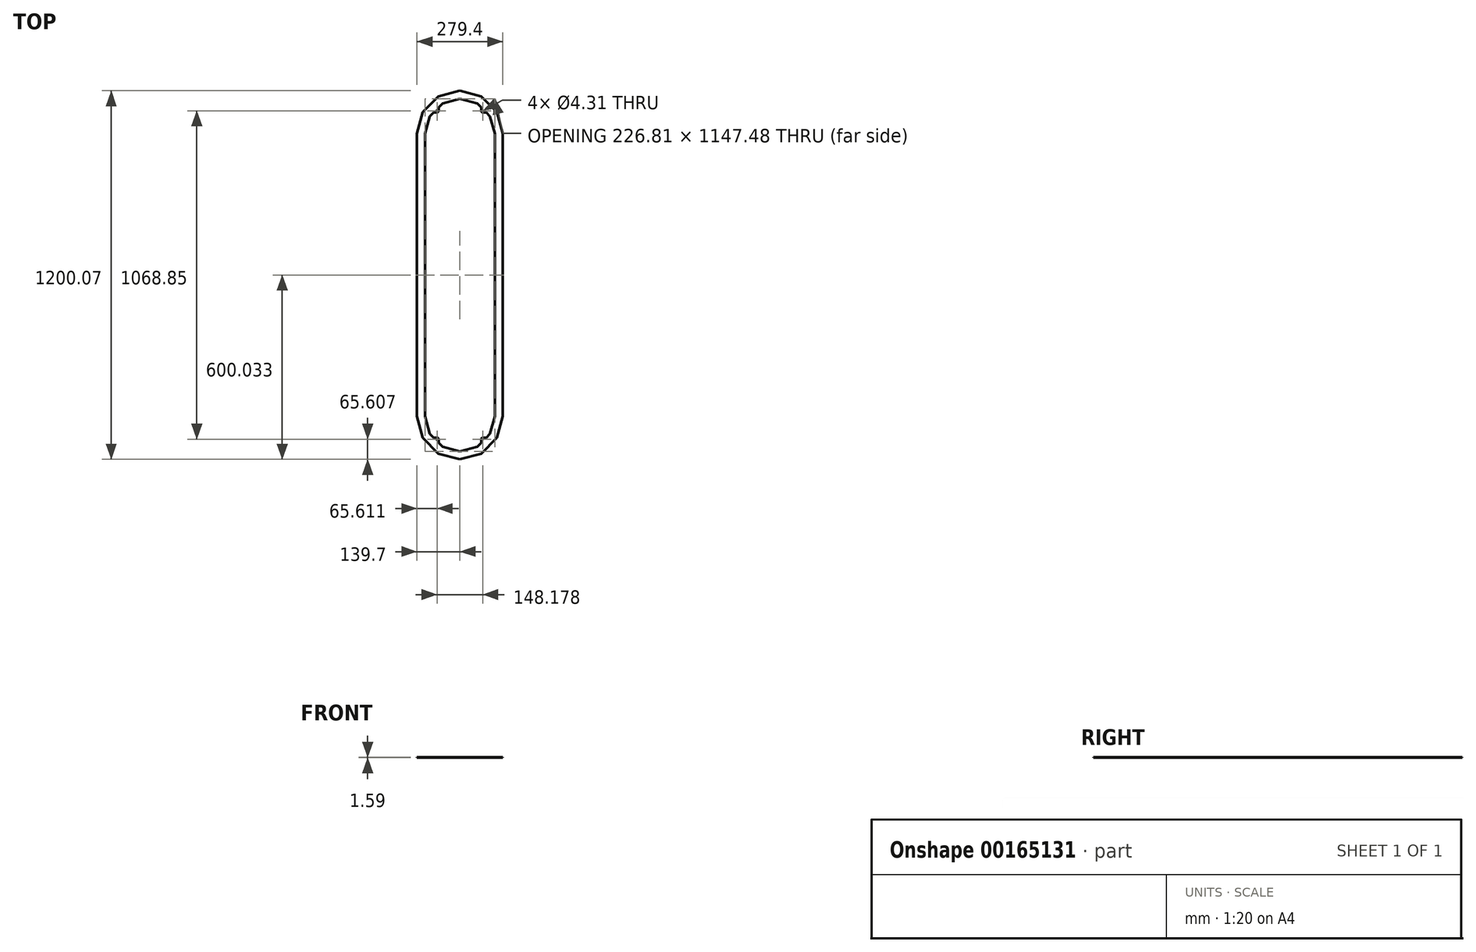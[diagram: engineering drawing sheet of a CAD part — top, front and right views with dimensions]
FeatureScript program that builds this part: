
annotation { "Feature Type Name" : "Feature", "Feature Type Description" : "" }
export const myFeature = defineFeature(function(context is Context, id is Id, definition is map)
    precondition{}
    {
        {
            var Q0;
            Q0=qCreatedBy(makeId("Top.planeOp"),FACE);
            var sketch = newSketch(context, id + "F0", { "sketchPlane" : qUnion([Q0])});
            skLineSegment(sketch, "E0", {"start": v(139.7, 0) * mm, "end": v(279.4, 0) * mm, "construction": true});
            skLineSegment(sketch, "E1", {"start": v(139.7, 0) * mm, "end": v(260.68, 69.85) * mm, "construction": true});
            skLineSegment(sketch, "E2", {"start": v(139.7, 0) * mm, "end": v(209.55, 120.98) * mm, "construction": true});
            skLineSegment(sketch, "E3", {"start": v(139.7, 0) * mm, "end": v(139.7, 139.7) * mm, "construction": true});
            skLineSegment(sketch, "E4", {"start": v(279.4, 0) * mm, "end": v(260.68, 69.85) * mm});
            skLineSegment(sketch, "E5", {"start": v(260.68, 69.85) * mm, "end": v(209.55, 120.98) * mm});
            skLineSegment(sketch, "E6", {"start": v(209.55, 120.98) * mm, "end": v(139.7, 139.7) * mm});
            skLineSegment(sketch, "E7", {"start": v(279.4, 0) * mm, "end": v(279.4, -920.67) * mm});
            skLineSegment(sketch, "E8", {"start": v(279.4, -920.67) * mm, "end": v(139.7, -920.67) * mm, "construction": true});
            skLineSegment(sketch, "E9", {"start": v(139.7, -920.67) * mm, "end": v(260.68, -990.52) * mm, "construction": true});
            skLineSegment(sketch, "E10", {"start": v(139.7, 0) * mm, "end": v(69.85, 120.98) * mm, "construction": true});
            skLineSegment(sketch, "E11", {"start": v(139.7, 0) * mm, "end": v(18.72, 69.85) * mm, "construction": true});
            skLineSegment(sketch, "E12", {"start": v(139.7, 0) * mm, "end": v(0, 0) * mm, "construction": true});
            skLineSegment(sketch, "E13", {"start": v(139.7, -920.67) * mm, "end": v(0, -920.67) * mm, "construction": true});
            skLineSegment(sketch, "E14", {"start": v(139.7, 139.7) * mm, "end": v(69.85, 120.98) * mm});
            skLineSegment(sketch, "E15", {"start": v(69.85, 120.98) * mm, "end": v(18.72, 69.85) * mm});
            skLineSegment(sketch, "E16", {"start": v(18.72, 69.85) * mm, "end": v(0, 0) * mm});
            skLineSegment(sketch, "E17", {"start": v(0, 0) * mm, "end": v(0, -920.67) * mm});
            skLineSegment(sketch, "E18", {"start": v(139.7, -920.67) * mm, "end": v(209.55, -1041.66) * mm, "construction": true});
            skLineSegment(sketch, "E19", {"start": v(139.7, -920.67) * mm, "end": v(139.7, -1060.37) * mm, "construction": true});
            skLineSegment(sketch, "E20", {"start": v(139.7, -920.67) * mm, "end": v(69.85, -1041.66) * mm, "construction": true});
            skLineSegment(sketch, "E21", {"start": v(139.7, -920.67) * mm, "end": v(18.72, -990.52) * mm, "construction": true});
            skLineSegment(sketch, "E22", {"start": v(0, -920.67) * mm, "end": v(18.72, -990.52) * mm});
            skLineSegment(sketch, "E23", {"start": v(18.72, -990.52) * mm, "end": v(69.85, -1041.66) * mm});
            skLineSegment(sketch, "E24", {"start": v(69.85, -1041.66) * mm, "end": v(139.7, -1060.37) * mm});
            skLineSegment(sketch, "E25", {"start": v(139.7, -1060.37) * mm, "end": v(209.55, -1041.66) * mm});
            skLineSegment(sketch, "E26", {"start": v(209.55, -1041.66) * mm, "end": v(260.68, -990.52) * mm});
            skLineSegment(sketch, "E27", {"start": v(260.68, -990.52) * mm, "end": v(279.4, -920.67) * mm});
            skLineSegment(sketch, "E28", {"start": v(139.7, 0) * mm, "end": v(139.7, -460.34) * mm, "construction": true});
            skLineSegment(sketch, "E29", {"start": v(139.7, -460.34) * mm, "end": v(139.7, -920.67) * mm, "construction": true});
            skSolve(sketch);
        }
        {
            var Q0;
            Q0=qSketchRegion(id+"F0",true);
            extrude(context, id + "F1", {"entities" : qUnion([Q0]), "depth" : 1.59 * mm});
        }
        {
            var Q0;
            Q0=makeQuery(id+"F1.opExtrude","CAP_FACE",FACE,{"disambiguationData":[OSD([sQuery(id+"F0.wireOp",EDGE,"E4"),sQuery(id+"F0.wireOp",EDGE,"E5"),sQuery(id+"F0.wireOp",EDGE,"E6"),sQuery(id+"F0.wireOp",EDGE,"E7"),sQuery(id+"F0.wireOp",EDGE,"E14"),sQuery(id+"F0.wireOp",EDGE,"E15"),sQuery(id+"F0.wireOp",EDGE,"E16"),sQuery(id+"F0.wireOp",EDGE,"E17"),sQuery(id+"F0.wireOp",EDGE,"E22"),sQuery(id+"F0.wireOp",EDGE,"E23"),sQuery(id+"F0.wireOp",EDGE,"E24"),sQuery(id+"F0.wireOp",EDGE,"E25"),sQuery(id+"F0.wireOp",EDGE,"E26"),sQuery(id+"F0.wireOp",EDGE,"E27")])],"isStart":false});
            var sketch = newSketch(context, id + "F2", { "sketchPlane" : qUnion([Q0])});
            skLineSegment(sketch, "E30", {"start": v(139.7, 0) * mm, "end": v(253.1, 0) * mm, "construction": true});
            skLineSegment(sketch, "E31", {"start": v(139.7, 0) * mm, "end": v(237.91, 56.7) * mm, "construction": true});
            skLineSegment(sketch, "E32", {"start": v(139.7, 0) * mm, "end": v(196.4, 98.21) * mm, "construction": true});
            skLineSegment(sketch, "E33", {"start": v(139.7, 0) * mm, "end": v(139.7, 113.4) * mm, "construction": true});
            skLineSegment(sketch, "E34", {"start": v(253.1, 0) * mm, "end": v(237.91, 56.7) * mm});
            skLineSegment(sketch, "E35", {"start": v(237.91, 56.7) * mm, "end": v(196.4, 98.21) * mm});
            skLineSegment(sketch, "E36", {"start": v(196.4, 98.21) * mm, "end": v(139.7, 113.4) * mm});
            skLineSegment(sketch, "E37", {"start": v(253.1, 0) * mm, "end": v(253.1, -920.67) * mm});
            skLineSegment(sketch, "E38", {"start": v(253.1, -920.67) * mm, "end": v(139.7, -920.67) * mm, "construction": true});
            skLineSegment(sketch, "E39", {"start": v(139.7, -920.67) * mm, "end": v(237.91, -977.38) * mm, "construction": true});
            skLineSegment(sketch, "E40", {"start": v(139.7, 0) * mm, "end": v(83, 98.21) * mm, "construction": true});
            skLineSegment(sketch, "E41", {"start": v(139.7, 0) * mm, "end": v(41.49, 56.7) * mm, "construction": true});
            skLineSegment(sketch, "E42", {"start": v(139.7, 0) * mm, "end": v(26.3, 0) * mm, "construction": true});
            skLineSegment(sketch, "E43", {"start": v(139.7, -920.67) * mm, "end": v(26.3, -920.67) * mm, "construction": true});
            skLineSegment(sketch, "E44", {"start": v(139.7, 113.4) * mm, "end": v(83, 98.21) * mm});
            skLineSegment(sketch, "E45", {"start": v(83, 98.21) * mm, "end": v(41.49, 56.7) * mm});
            skLineSegment(sketch, "E46", {"start": v(41.49, 56.7) * mm, "end": v(26.3, 0) * mm});
            skLineSegment(sketch, "E47", {"start": v(26.3, 0) * mm, "end": v(26.3, -920.67) * mm});
            skLineSegment(sketch, "E48", {"start": v(139.7, -920.67) * mm, "end": v(196.4, -1018.89) * mm, "construction": true});
            skLineSegment(sketch, "E49", {"start": v(139.7, -920.67) * mm, "end": v(139.7, -1034.08) * mm, "construction": true});
            skLineSegment(sketch, "E50", {"start": v(139.7, -920.67) * mm, "end": v(83, -1018.89) * mm, "construction": true});
            skLineSegment(sketch, "E51", {"start": v(139.7, -920.67) * mm, "end": v(41.49, -977.38) * mm, "construction": true});
            skLineSegment(sketch, "E52", {"start": v(26.3, -920.67) * mm, "end": v(41.49, -977.38) * mm});
            skLineSegment(sketch, "E53", {"start": v(41.49, -977.38) * mm, "end": v(83, -1018.89) * mm});
            skLineSegment(sketch, "E54", {"start": v(83, -1018.89) * mm, "end": v(139.7, -1034.08) * mm});
            skLineSegment(sketch, "E55", {"start": v(139.7, -1034.08) * mm, "end": v(196.4, -1018.89) * mm});
            skLineSegment(sketch, "E56", {"start": v(196.4, -1018.89) * mm, "end": v(237.91, -977.38) * mm});
            skLineSegment(sketch, "E57", {"start": v(237.91, -977.38) * mm, "end": v(253.1, -920.67) * mm});
            skLineSegment(sketch, "E58", {"start": v(139.7, 0) * mm, "end": v(139.7, -460.34) * mm, "construction": true});
            skLineSegment(sketch, "E59", {"start": v(139.7, -460.34) * mm, "end": v(139.7, -920.67) * mm, "construction": true});
            skLineSegment(sketch, "E60", {"start": v(33.9, 28.35) * mm, "end": v(9.36, 34.93) * mm, "construction": true});
            skLineSegment(sketch, "E61", {"start": v(245.5, 28.35) * mm, "end": v(270.04, 34.93) * mm, "construction": true});
            skLineSegment(sketch, "E62", {"start": v(33.9, -949.03) * mm, "end": v(9.36, -955.6) * mm, "construction": true});
            skLineSegment(sketch, "E63", {"start": v(245.5, -949.03) * mm, "end": v(270.04, -955.6) * mm, "construction": true});
            skSolve(sketch);
        }
        {
            var Q0;
            Q0 = qSketchRegion(id + "F2", true);
            var Q1;
            Q1=makeQuery(id+"F1.opExtrude","CAP_FACE",FACE,{"disambiguationData":[OSD([sQuery(id+"F0.wireOp",EDGE,"E4"),sQuery(id+"F0.wireOp",EDGE,"E5"),sQuery(id+"F0.wireOp",EDGE,"E6"),sQuery(id+"F0.wireOp",EDGE,"E7"),sQuery(id+"F0.wireOp",EDGE,"E14"),sQuery(id+"F0.wireOp",EDGE,"E15"),sQuery(id+"F0.wireOp",EDGE,"E16"),sQuery(id+"F0.wireOp",EDGE,"E17"),sQuery(id+"F0.wireOp",EDGE,"E22"),sQuery(id+"F0.wireOp",EDGE,"E23"),sQuery(id+"F0.wireOp",EDGE,"E24"),sQuery(id+"F0.wireOp",EDGE,"E25"),sQuery(id+"F0.wireOp",EDGE,"E26"),sQuery(id+"F0.wireOp",EDGE,"E27")])],"isStart":true});
            extrude(context, id + "F3", {"entities" : qUnion([Q0]), "operationType" : NewBodyOperationType.REMOVE, "endBound" : BoundingType.UP_TO_SURFACE, "oppositeDirection" : true, "endBoundEntityFace" : qUnion([Q1]), "depth" : 25.4 * mm});
        }
        {
            var Q0;
            Q0=makeQuery(id+"F1.opExtrude","CAP_FACE",FACE,{"disambiguationData":[OSD([sQuery(id+"F0.wireOp",EDGE,"E4"),sQuery(id+"F0.wireOp",EDGE,"E5"),sQuery(id+"F0.wireOp",EDGE,"E6"),sQuery(id+"F0.wireOp",EDGE,"E7"),sQuery(id+"F0.wireOp",EDGE,"E14"),sQuery(id+"F0.wireOp",EDGE,"E15"),sQuery(id+"F0.wireOp",EDGE,"E16"),sQuery(id+"F0.wireOp",EDGE,"E17"),sQuery(id+"F0.wireOp",EDGE,"E22"),sQuery(id+"F0.wireOp",EDGE,"E23"),sQuery(id+"F0.wireOp",EDGE,"E24"),sQuery(id+"F0.wireOp",EDGE,"E25"),sQuery(id+"F0.wireOp",EDGE,"E26"),sQuery(id+"F0.wireOp",EDGE,"E27")])],"isStart":false});
            var sketch = newSketch(context, id + "F4", { "sketchPlane" : qUnion([Q0])});
            skLineSegment(sketch, "E64.bottom", {"start": v(213.79, 74.09) * mm, "end": v(65.61, 74.09) * mm, "construction": true});
            skLineSegment(sketch, "E64.top", {"start": v(213.79, -994.76) * mm, "end": v(65.61, -994.76) * mm, "construction": true});
            skLineSegment(sketch, "E64.left", {"start": v(213.79, 74.09) * mm, "end": v(213.79, -994.76) * mm, "construction": true});
            skLineSegment(sketch, "E64.right", {"start": v(65.61, 74.09) * mm, "end": v(65.61, -994.76) * mm, "construction": true});
            skPoint(sketch, "E64.middle", {"position": v(139.7, -460.34) * mm});
            skLineSegment(sketch, "E65", {"start": v(139.7, 113.4) * mm, "end": v(139.7, -1034.08) * mm, "construction": true});
            skLineSegment(sketch, "E66.bottom", {"start": v(209.03, 85.59) * mm, "end": v(209.03, 74.09) * mm});
            skLineSegment(sketch, "E66.top", {"start": v(225.29, 69.33) * mm, "end": v(213.79, 69.33) * mm});
            skLineSegment(sketch, "E66.left", {"start": v(209.03, 85.59) * mm, "end": v(225.29, 69.33) * mm});
            skLineSegment(sketch, "E67.bottom", {"start": v(70.37, 74.09) * mm, "end": v(70.37, 85.59) * mm});
            skLineSegment(sketch, "E67.top", {"start": v(65.61, 69.33) * mm, "end": v(54.11, 69.33) * mm});
            skLineSegment(sketch, "E67.right", {"start": v(70.37, 85.59) * mm, "end": v(54.11, 69.33) * mm});
            skArc(sketch, "E68", {"start": v(65.61, 69.33) * mm, "mid": v(68.98, 70.72) * mm, "end": v(70.37, 74.09) * mm});
            skArc(sketch, "E69", {"start": v(209.03, 74.09) * mm, "mid": v(210.42, 70.72) * mm, "end": v(213.79, 69.33) * mm});
            skLineSegment(sketch, "E70.bottom", {"start": v(54.11, -990) * mm, "end": v(70.37, -1006.26) * mm});
            skLineSegment(sketch, "E70.left", {"start": v(70.37, -1006.26) * mm, "end": v(70.37, -994.76) * mm});
            skLineSegment(sketch, "E70.right", {"start": v(54.11, -990) * mm, "end": v(65.61, -990) * mm});
            skLineSegment(sketch, "E71.bottom", {"start": v(225.29, -990) * mm, "end": v(209.03, -1006.26) * mm});
            skLineSegment(sketch, "E71.left", {"start": v(225.29, -990) * mm, "end": v(213.79, -990) * mm});
            skLineSegment(sketch, "E71.right", {"start": v(209.03, -1006.26) * mm, "end": v(209.03, -994.76) * mm});
            skArc(sketch, "E72", {"start": v(70.37, -994.76) * mm, "mid": v(68.98, -991.4) * mm, "end": v(65.61, -990) * mm});
            skArc(sketch, "E73", {"start": v(213.79, -990) * mm, "mid": v(210.42, -991.4) * mm, "end": v(209.03, -994.76) * mm});
            skCircle(sketch, "E74", {"center": v(213.79, -994.76) * mm, "radius": 2.15 * mm});
            skCircle(sketch, "E75", {"center": v(65.61, -994.76) * mm, "radius": 2.15 * mm});
            skCircle(sketch, "E76", {"center": v(213.79, 74.09) * mm, "radius": 2.15 * mm});
            skCircle(sketch, "E77", {"center": v(65.61, 74.09) * mm, "radius": 2.15 * mm});
            skArc(sketch, "E78", {"start": v(65.61, -990) * mm, "mid": v(62.24, -998.13) * mm, "end": v(70.37, -994.76) * mm, "construction": true});
            skPoint(sketch, "E79", {"position": v(62.24, -998.13) * mm});
            skPoint(sketch, "E80", {"position": v(217.16, -998.13) * mm});
            skPoint(sketch, "E81", {"position": v(217.16, 77.46) * mm});
            skPoint(sketch, "E82", {"position": v(62.24, 77.46) * mm});
            skSolve(sketch);
        }
        {
            var Q0;
            Q0 = qSketchRegion(id + "F4", true);
            var Q1;
            Q1=makeQuery(id+"F1.opExtrude","CAP_FACE",FACE,{"disambiguationData":[OSD([sQuery(id+"F0.wireOp",EDGE,"E4"),sQuery(id+"F0.wireOp",EDGE,"E5"),sQuery(id+"F0.wireOp",EDGE,"E6"),sQuery(id+"F0.wireOp",EDGE,"E7"),sQuery(id+"F0.wireOp",EDGE,"E14"),sQuery(id+"F0.wireOp",EDGE,"E15"),sQuery(id+"F0.wireOp",EDGE,"E16"),sQuery(id+"F0.wireOp",EDGE,"E17"),sQuery(id+"F0.wireOp",EDGE,"E22"),sQuery(id+"F0.wireOp",EDGE,"E23"),sQuery(id+"F0.wireOp",EDGE,"E24"),sQuery(id+"F0.wireOp",EDGE,"E25"),sQuery(id+"F0.wireOp",EDGE,"E26"),sQuery(id+"F0.wireOp",EDGE,"E27")])],"isStart":true});
            extrude(context, id + "F5", {"entities" : qUnion([Q0]), "operationType" : NewBodyOperationType.ADD, "endBound" : BoundingType.UP_TO_SURFACE, "oppositeDirection" : true, "endBoundEntityFace" : qUnion([Q1]), "depth" : 25.4 * mm});
        }
    });
